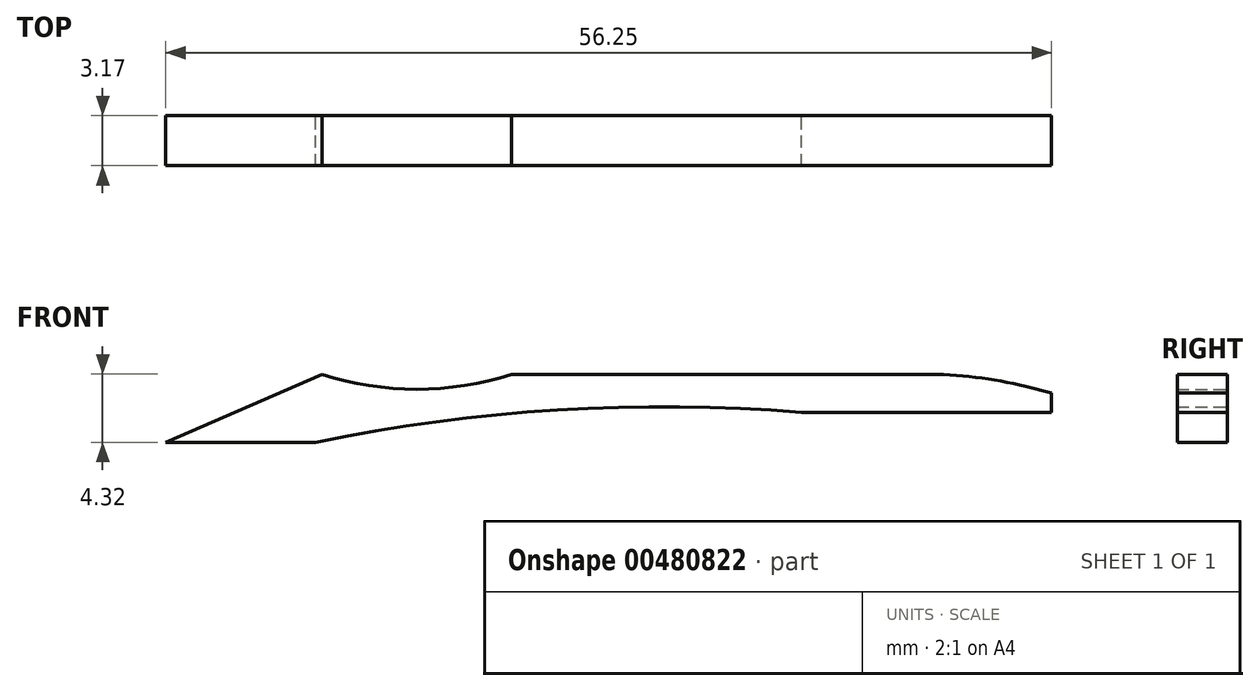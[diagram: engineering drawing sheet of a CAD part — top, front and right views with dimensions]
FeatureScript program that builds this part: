
annotation { "Feature Type Name" : "Feature", "Feature Type Description" : "" }
export const myFeature = defineFeature(function(context is Context, id is Id, definition is map)
    precondition{}
    {
        {
            var Q0;
            Q0=qCreatedBy(makeId("Front.planeOp"),FACE);
            var sketch = newSketch(context, id + "F0", { "sketchPlane" : qUnion([Q0])});
            skLineSegment(sketch, "E0", {"start": v(-64.52, 0) * mm, "end": v(-54.6, 4.32) * mm});
            skLineSegment(sketch, "E1", {"start": v(-64.52, 0) * mm, "end": v(-55, 0) * mm});
            skArc(sketch, "E2", {"start": v(-54.6, 4.32) * mm, "mid": v(-48.58, 3.36) * mm, "end": v(-42.56, 4.32) * mm});
            skLineSegment(sketch, "E3", {"start": v(-42.56, 4.32) * mm, "end": v(-16.33, 4.32) * mm});
            skLineSegment(sketch, "E4", {"start": v(-9.9, 3.54) * mm, "end": v(-8.27, 3.14) * mm});
            skLineSegment(sketch, "E5", {"start": v(-8.27, 3.14) * mm, "end": v(-8.27, 1.9) * mm});
            skLineSegment(sketch, "E6", {"start": v(-8.27, 1.9) * mm, "end": v(-24.15, 1.9) * mm});
            skArc(sketch, "E7", {"start": v(-24.15, 1.9) * mm, "mid": v(-39.64, 2.04) * mm, "end": v(-55, 0) * mm});
            skPoint(sketch, "E8.visualSharp", {"position": v(-13.06, 4.32) * mm});
            skArc(sketch, "E8.filletArc", {"start": v(-9.9, 3.54) * mm, "mid": v(-13.09, 4.12) * mm, "end": v(-16.33, 4.32) * mm});
            skSolve(sketch);
        }
        {
            var Q0;
            Q0=makeQuery(id+"F0.imprint","IMPRINT",FACE,{"disambiguationData":[TD([[makeQuery(id+"F0.imprint","IMPRINT",EDGE,{"derivedFrom":sQuery(id+"F0.wireOp",EDGE,"E0")}),-1.0]])]});
            extrude(context, id + "F1", {"entities" : qUnion([Q0]), "depth" : 3.17 * mm});
        }
    });
